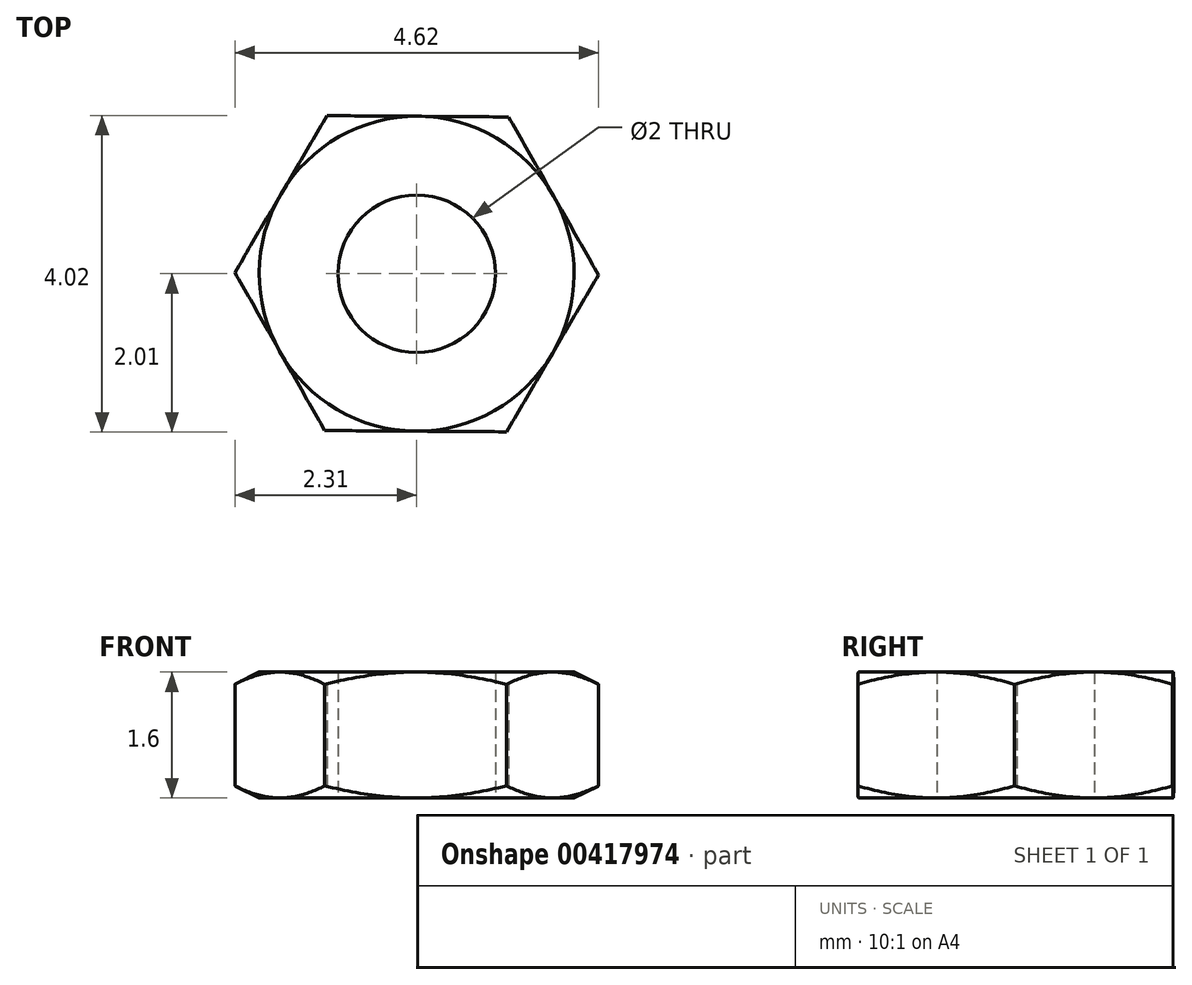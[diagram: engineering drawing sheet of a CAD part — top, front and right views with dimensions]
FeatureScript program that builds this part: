
annotation { "Feature Type Name" : "Feature", "Feature Type Description" : "" }
export const myFeature = defineFeature(function(context is Context, id is Id, definition is map)
    precondition{}
    {
        {
            var Q0;
            Q0=qCreatedBy(makeId("Top.planeOp"),FACE);
            var sketch = newSketch(context, id + "F0", { "sketchPlane" : qUnion([Q0])});
            skCircle(sketch, "E0.cCircle", {"center": v(0, 0) * mm, "radius": 2 * mm, "construction": true});
            skLineSegment(sketch, "E0.0", {"start": v(2.3, -0.02) * mm, "end": v(1.14, -2) * mm});
            skLineSegment(sketch, "E0.1", {"start": v(1.14, -2) * mm, "end": v(-1.17, -2) * mm});
            skLineSegment(sketch, "E0.2", {"start": v(-1.17, -2) * mm, "end": v(-2.3, 0.02) * mm});
            skLineSegment(sketch, "E0.3", {"start": v(-2.3, 0.02) * mm, "end": v(-1.14, 2) * mm});
            skLineSegment(sketch, "E0.4", {"start": v(-1.14, 2) * mm, "end": v(1.17, 2) * mm});
            skLineSegment(sketch, "E0.5", {"start": v(1.17, 2) * mm, "end": v(2.3, -0.02) * mm});
            skPoint(sketch, "E0.0.midPoint", {"position": v(1.72, -1.01) * mm});
            skCircle(sketch, "E1", {"center": v(0, 0) * mm, "radius": 1 * mm});
            skSolve(sketch);
        }
        {
            var Q0;
            Q0 = qSketchRegion(id + "F0", true);
            extrude(context, id + "F1", {"entities" : qUnion([Q0]), "depth" : 1.6 * mm});
        }
        {
            var Q0;
            Q0=makeQuery(id+"F1.opExtrude","CAP_EDGE",EDGE,{"disambiguationData":[OSD([sQuery(id+"F0.wireOp",EDGE,"E0.0")])],"isStart":false});
            cPoint(context, id + "F2", {"entities" : qUnion([Q0]), "parameter" : 0.5});
        }
        {
            var Q0;
            Q0=makeQuery(id+"F1.opExtrude","CAP_EDGE",EDGE,{"disambiguationData":[OSD([sQuery(id+"F0.wireOp",EDGE,"E0.0")])],"isStart":true});
            cPoint(context, id + "F3", {"entities" : qUnion([Q0]), "parameter" : 0.5});
        }
        {
            var Q0;
            Q0=makeQuery(id+"F1.opExtrude","CAP_EDGE",EDGE,{"disambiguationData":[OSD([sQuery(id+"F0.wireOp",EDGE,"E0.3")])],"isStart":false});
            cPoint(context, id + "F4", {"entities" : qUnion([Q0]), "parameter" : 0.5});
        }
        {
            var Q0;
            Q0 = qCreatedBy(id + "F2" ,VERTEX);
            var Q1;
            Q1 = qCreatedBy(id + "F3" ,VERTEX);
            var Q2;
            Q2 = qCreatedBy(id + "F4" ,VERTEX);
            cPlane(context, id + "F5", {"entities" : qUnion([Q0, Q1, Q2]), "cplaneType" : CPlaneType.THREE_POINT, "offset" : 25 * mm, "width" : 150 * mm, "height" : 150 * mm});
        }
        {
            var Q0;
            Q0=qCreatedBy(id+"F5.planeOp",FACE);
            var sketch = newSketch(context, id + "F6", { "sketchPlane" : qUnion([Q0])});
            skLineSegment(sketch, "E2", {"start": v(2, 1.6) * mm, "end": v(3, 1.6) * mm});
            skLineSegment(sketch, "E3", {"start": v(3, 1.6) * mm, "end": v(3, 1.1) * mm});
            skLineSegment(sketch, "E4", {"start": v(3, 1.1) * mm, "end": v(2, 1.6) * mm});
            skLineSegment(sketch, "E5", {"start": v(2, 0) * mm, "end": v(3, 0) * mm});
            skLineSegment(sketch, "E6", {"start": v(3, 0) * mm, "end": v(3, 0.5) * mm});
            skLineSegment(sketch, "E7", {"start": v(3, 0.5) * mm, "end": v(2, 0) * mm});
            skLineSegment(sketch, "E8", {"start": v(0, 3.95) * mm, "end": v(0, -3.49) * mm, "construction": true});
            skPoint(sketch, "E9.orphan", {"position": v(0, 3.45) * mm});
            skSolve(sketch);
        }
        {
            var Q0;
            Q0 = qSketchRegion(id + "F6", true);
            var Q1;
            Q1=sQuery(id+"F6.wireOp",EDGE,"E8");
            revolve(context, id + "F7", {"operationType" : NewBodyOperationType.REMOVE, "entities" : qUnion([Q0]), "axis" : qUnion([Q1]), "revolveType" : RevolveType.FULL, "oppositeDirection" : true});
        }
    });
